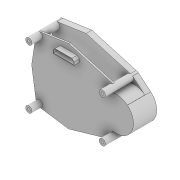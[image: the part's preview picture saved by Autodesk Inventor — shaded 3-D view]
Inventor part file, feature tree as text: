
AUTODESK INVENTOR PART (.ipt)
format: ipt  version: 2020 (Build 240168000, 168)  size: 306,176 bytes
history: native  units: mm
features: extrude x7, sketch x7, projected_geometry x7, other x1
ambient origin geometry x8: Origin, YZ Plane, XZ Plane, XY Plane, X Axis, Y Axis, Z Axis, Center Point
bodies: Body1 (feature_tree)
feature tree (22):
  other  "솔리드1"
  extrude  "돌출1"  Depth=35.14mm
  extrude  "돌출2"  Depth=96.74mm
  extrude  "돌출3"  Depth=70.28mm
  extrude  "돌출4"  Depth=27.87mm
  extrude  "돌출5"  Depth=42.0mm
  extrude  "돌출6"  Depth=40.0mm
  extrude  "돌출7"  Depth=2.5mm
  sketch  "스케치1"
  sketch  "스케치2"
  sketch  "스케치3"
  sketch  "스케치4"
  sketch  "스케치5"
  projected_geometry  "투영된 루프1"
  sketch  "스케치6"
  projected_geometry  "투영된 루프2"
  projected_geometry  "투영된 루프3"
  projected_geometry  "투영된 루프4"
  projected_geometry  "투영된 루프5"
  projected_geometry  "투영된 루프6"
  sketch  "스케치7"
  projected_geometry  "투영된 루프7"
